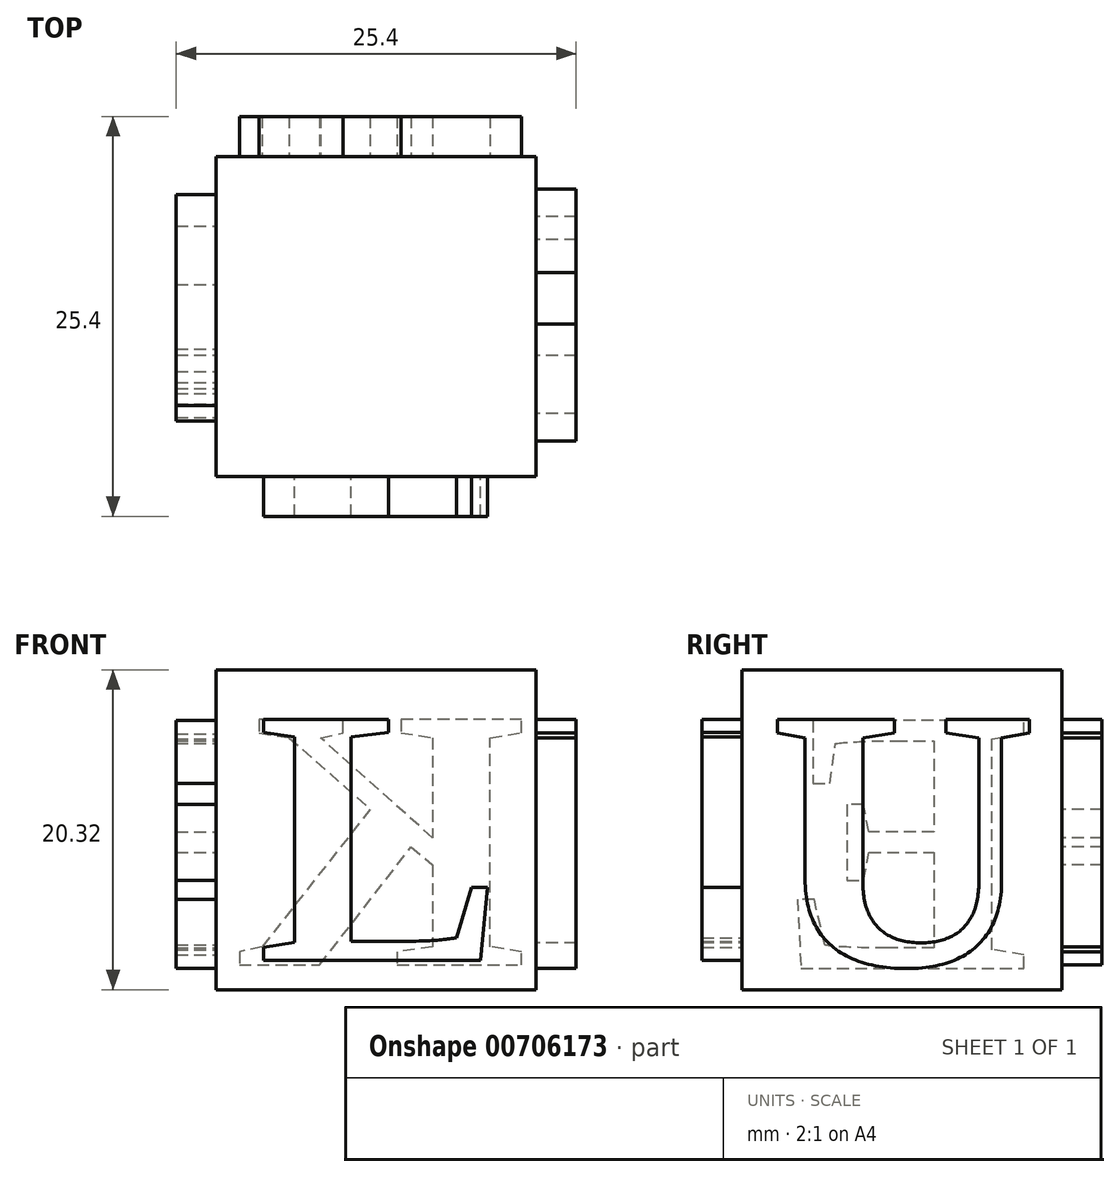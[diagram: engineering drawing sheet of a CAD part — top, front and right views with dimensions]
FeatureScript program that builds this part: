
annotation { "Feature Type Name" : "Feature", "Feature Type Description" : "" }
export const myFeature = defineFeature(function(context is Context, id is Id, definition is map)
    precondition{}
    {
        {
            var Q0;
            Q0=qCreatedBy(makeId("Front.planeOp"),FACE);
            var sketch = newSketch(context, id + "F0", { "sketchPlane" : qUnion([Q0])});
            skLineSegment(sketch, "E0.bottom", {"start": v(-10.16, 10.16) * mm, "end": v(10.16, 10.16) * mm});
            skLineSegment(sketch, "E0.top", {"start": v(-10.16, -10.16) * mm, "end": v(10.16, -10.16) * mm});
            skLineSegment(sketch, "E0.left", {"start": v(-10.16, 10.16) * mm, "end": v(-10.16, -10.16) * mm});
            skLineSegment(sketch, "E0.right", {"start": v(10.16, 10.16) * mm, "end": v(10.16, -10.16) * mm});
            skPoint(sketch, "E0.middle", {"position": v(0, 0) * mm});
            skSolve(sketch);
        }
        {
            var Q0;
            Q0 = qSketchRegion(id + "F0", true);
            extrude(context, id + "F1", {"entities" : qUnion([Q0]), "depth" : 20.32 * mm, "offsetDistance" : 25.4 * mm});
        }
        {
            var Q0;
            Q0=makeQuery(id+"F1.opExtrude","CAP_FACE",FACE,{"disambiguationData":[OSD([sQuery(id+"F0.wireOp",EDGE,"E0.bottom"),sQuery(id+"F0.wireOp",EDGE,"E0.top"),sQuery(id+"F0.wireOp",EDGE,"E0.left"),sQuery(id+"F0.wireOp",EDGE,"E0.right")])],"isStart":false});
            var sketch = newSketch(context, id + "F2", { "sketchPlane" : qUnion([Q0])});
            skText(sketch, "E1", { "text": "L", "fontName": "Tinos-Bold.ttf"});
            const initialGuessF2  = {"E1": [-0.00755, -0.0083, 1, 0, 0.01684]};
            skSetInitialGuess(sketch, initialGuessF2);
            skSolve(sketch);
        }
        {
            var Q0;
            Q0 = qSketchRegion(id + "F2", true);
            extrude(context, id + "F3", {"entities" : qUnion([Q0]), "operationType" : NewBodyOperationType.ADD, "depth" : 2.54 * mm, "offsetDistance" : 25.4 * mm});
        }
        {
            var Q0;
            Q0=makeQuery(id+"F1.opExtrude","SWEPT_FACE",FACE,{"disambiguationData":[OSD([sQuery(id+"F0.wireOp",EDGE,"E0.right")])]});
            var sketch = newSketch(context, id + "F4", { "sketchPlane" : qUnion([Q0])});
            skText(sketch, "E2", { "text": "U", "fontName": "Tinos-Bold.ttf"});
            const initialGuessF4  = {"E2": [-0.01868, -0.0086, 1, 0, 0.01715]};
            skSetInitialGuess(sketch, initialGuessF4);
            skSolve(sketch);
        }
        {
            var Q0;
            Q0 = qSketchRegion(id + "F4", true);
            extrude(context, id + "F5", {"entities" : qUnion([Q0]), "operationType" : NewBodyOperationType.ADD, "depth" : 2.54 * mm, "offsetDistance" : 25.4 * mm});
        }
        {
            var Q0;
            Q0=makeQuery(id+"F1.opExtrude","CAP_FACE",FACE,{"disambiguationData":[OSD([sQuery(id+"F0.wireOp",EDGE,"E0.bottom"),sQuery(id+"F0.wireOp",EDGE,"E0.top"),sQuery(id+"F0.wireOp",EDGE,"E0.left"),sQuery(id+"F0.wireOp",EDGE,"E0.right")])],"isStart":true});
            var sketch = newSketch(context, id + "F6", { "sketchPlane" : qUnion([Q0])});
            skText(sketch, "E3", { "text": "K", "fontName": "Tinos-Bold.ttf"});
            const initialGuessF6  = {"E3": [-0.00965, -0.0086, 1, 0, 0.01715]};
            skSetInitialGuess(sketch, initialGuessF6);
            skSolve(sketch);
        }
        {
            var Q0;
            Q0 = qSketchRegion(id + "F6", true);
            extrude(context, id + "F7", {"entities" : qUnion([Q0]), "operationType" : NewBodyOperationType.ADD, "depth" : 2.54 * mm, "offsetDistance" : 25.4 * mm});
        }
        {
            var Q0;
            Q0=makeQuery(id+"F1.opExtrude","SWEPT_FACE",FACE,{"disambiguationData":[OSD([sQuery(id+"F0.wireOp",EDGE,"E0.left")])]});
            var sketch = newSketch(context, id + "F8", { "sketchPlane" : qUnion([Q0])});
            skText(sketch, "E4", { "text": "E", "fontName": "Tinos-Bold.ttf"});
            skPoint(sketch, "E5", {"position": v(10.16, 10.16) * mm});
            const initialGuessF8  = {"E4": [0.00201, -0.0088, 1, 0, 0.0173]};
            skSetInitialGuess(sketch, initialGuessF8);
            skSolve(sketch);
        }
        {
            var Q0;
            Q0 = qSketchRegion(id + "F8", true);
            extrude(context, id + "F9", {"entities" : qUnion([Q0]), "operationType" : NewBodyOperationType.ADD, "depth" : 2.54 * mm, "offsetDistance" : 25.4 * mm});
        }
    });
